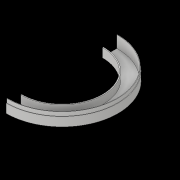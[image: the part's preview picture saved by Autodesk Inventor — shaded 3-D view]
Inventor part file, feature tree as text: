
AUTODESK INVENTOR PART (.ipt)
format: ipt  version: 2017 (Build 210142000, 142)  size: 122,368 bytes
history: native  units: in
note: dims shown in document units (in); Inventor stores cm internally (conversion verified against a paired STEP export)
features: revolve x1, sketch x1
ambient origin geometry x8: Origin, YZ Plane, XZ Plane, XY Plane, X Axis, Y Axis, Z Axis, Center Point
bodies: Solid1 (feature_tree)
feature tree (2):
  revolve  "Revolution1"  [1 undecoded]
  sketch  "Sketch1"  dims[d0=2.0in d2=10.5in d3=2.0in d4=2.875in d5=0.125in d6=0.125in d7=0.125in d8=0.125in d9=0.125in d10=0.125in d11=0.125in d12=0.125in d13=1.0285in d14=0.5in d15=180.0deg d16=5.25in d17=0.125in d18=0.125in d19=0.25in d20=0.0625in d21=0.25in d22=0.25in]
note: 1 required parameter value undecoded (feature->parameter linkage not recoverable at this tier; creation-order binding heuristic only, values carry confidence <= 0.55)
